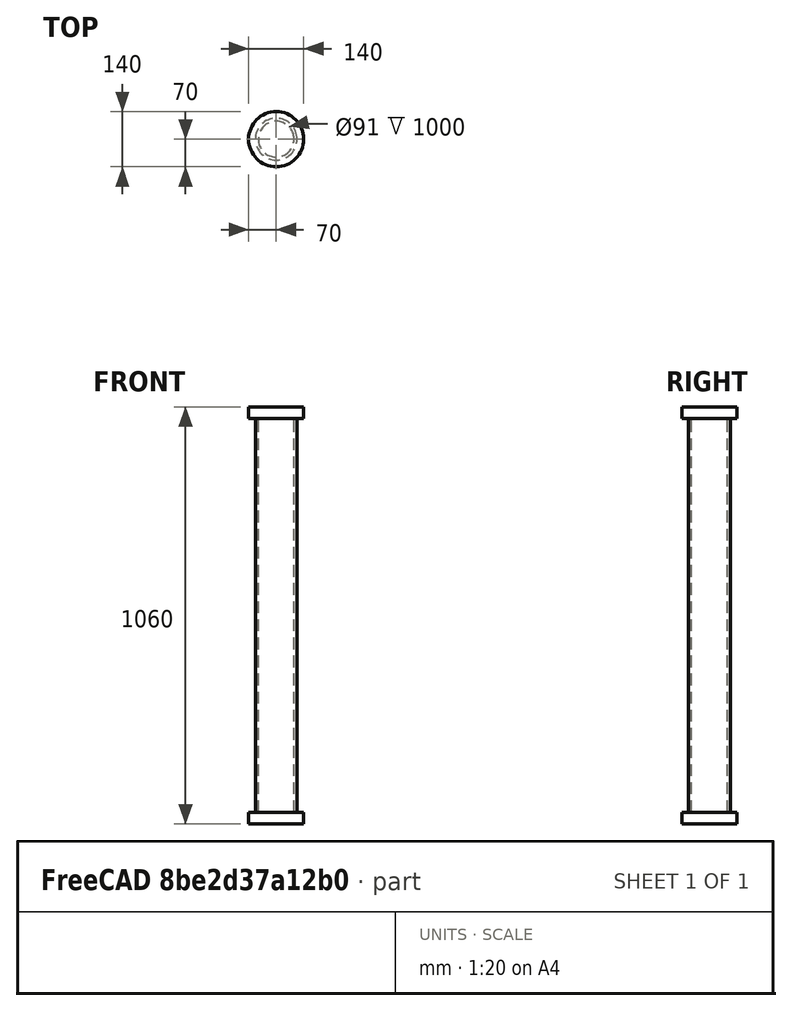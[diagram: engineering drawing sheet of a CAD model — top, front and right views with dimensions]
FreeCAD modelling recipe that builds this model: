
FCSTD DOCUMENT  (FreeCAD 0.19R)
Label: model
License: All rights reserved
LicenseURL: http://en.wikipedia.org/wiki/All_rights_reserved
objects: Mesh::Feature×3, Part::Cylinder×2, Part::FeaturePython×1
note: 3 computed .brp shape members not serialized (recipe doc carries the construction recipe); baked Part::Feature solids carry a one-line shape summary decoded from their .brp

FEATURE [Part::FeaturePython] Tube  # WARN: FeaturePython — macro-defined, semantics opaque (R4)
  AttacherType = Attacher::AttachEngine3D
  Height = 1000
  InnerRadius = 45.5
  OuterRadius = 53
FEATURE [Part::Cylinder] Cylinder001
  Angle = 360
  AttacherType = Attacher::AttachEngine3D
  Height = 30
  Placement = pos=(0,0,-30) rot=(0,0,1;0rad)
  Radius = 70
FEATURE [Part::Cylinder] Cylinder003
  Angle = 360
  AttacherType = Attacher::AttachEngine3D
  Height = 30
  Placement = pos=(0,0,1000) rot=(0,0,1;0rad)
  Radius = 70
FEATURE [Mesh::Feature] Mesh001  label="Cylinder001 (Meshed)"
FEATURE [Mesh::Feature] Mesh002  label="Cylinder003 (Meshed)"
FEATURE [Mesh::Feature] Mesh  label="Tube (Meshed)"
